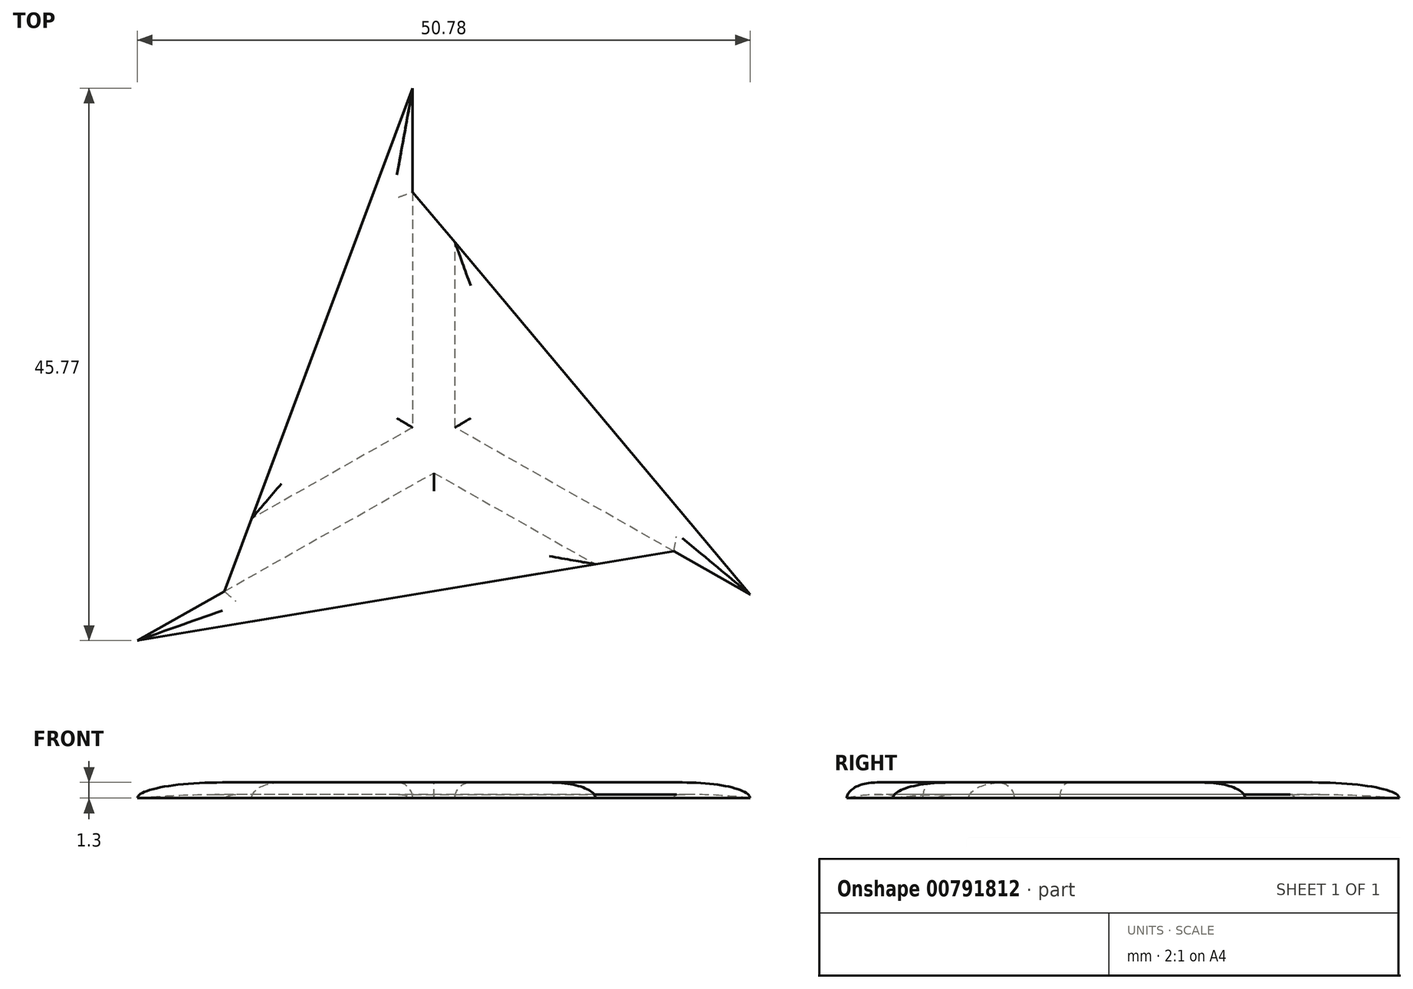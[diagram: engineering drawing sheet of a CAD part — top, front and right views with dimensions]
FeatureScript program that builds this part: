
annotation { "Feature Type Name" : "Feature", "Feature Type Description" : "" }
export const myFeature = defineFeature(function(context is Context, id is Id, definition is map)
    precondition{}
    {
        {
            var Q0;
            Q0=qCreatedBy(makeId("Top.planeOp"),FACE);
            var sketch = newSketch(context, id + "F0", { "sketchPlane" : qUnion([Q0])});
            skLineSegment(sketch, "E0.0", {"start": v(-37.37, 14.16) * mm, "end": v(-24.02, 49.82) * mm});
            skLineSegment(sketch, "E0.1", {"start": v(-24.02, 21.71) * mm, "end": v(-37.37, 14.16) * mm});
            skLineSegment(sketch, "E0.2", {"start": v(-24.02, 49.82) * mm, "end": v(-24.02, 21.71) * mm});
            skLineSegment(sketch, "E1.0", {"start": v(-20.52, 21.71) * mm, "end": v(-20.52, 37.04) * mm});
            skLineSegment(sketch, "E1.1", {"start": v(3.94, 7.87) * mm, "end": v(-20.52, 21.71) * mm});
            skLineSegment(sketch, "E1.2", {"start": v(-20.52, 37.04) * mm, "end": v(3.94, 7.87) * mm});
            skLineSegment(sketch, "E2.0", {"start": v(-46.84, 4.05) * mm, "end": v(-22.27, 17.95) * mm});
            skLineSegment(sketch, "E2.1", {"start": v(-8.87, 10.37) * mm, "end": v(-46.84, 4.05) * mm});
            skLineSegment(sketch, "E2.2", {"start": v(-22.27, 17.95) * mm, "end": v(-8.87, 10.37) * mm});
            skSolve(sketch);
        }
        {
            var Q0;
            Q0=qSketchRegion(id+"F0",true);
            extrude(context, id + "F1", {"entities" : qUnion([Q0]), "depth" : 1.3 * mm, "offsetDistance" : 25 * mm});
        }
        {
            var Q0;
            Q0=makeQuery(id+"F1.opExtrude","CAP_FACE",FACE,{"disambiguationData":[OSD([sQuery(id+"F0.wireOp",EDGE,"E0.0"),sQuery(id+"F0.wireOp",EDGE,"E0.1"),sQuery(id+"F0.wireOp",EDGE,"E0.2")])],"isStart":false});
            var Q1;
            Q1=makeQuery(id+"F1.opExtrude","CAP_FACE",FACE,{"disambiguationData":[OSD([sQuery(id+"F0.wireOp",EDGE,"E1.0"),sQuery(id+"F0.wireOp",EDGE,"E1.1"),sQuery(id+"F0.wireOp",EDGE,"E1.2")])],"isStart":false});
            var Q2;
            Q2=makeQuery(id+"F1.opExtrude","CAP_FACE",FACE,{"disambiguationData":[OSD([sQuery(id+"F0.wireOp",EDGE,"E2.0"),sQuery(id+"F0.wireOp",EDGE,"E2.1"),sQuery(id+"F0.wireOp",EDGE,"E2.2")])],"isStart":false});
            fillet(context, id + "F2", {"entities" : qUnion([Q0, Q1, Q2]), "radius" : 1.3 * mm, "tangentPropagation" : true, "allowEdgeOverflow" : false});
        }
        {
            var Q0;
            Q0=makeQuery(id+"F1.opExtrude","CAP_FACE",FACE,{"disambiguationData":[OSD([sQuery(id+"F0.wireOp",EDGE,"E0.0"),sQuery(id+"F0.wireOp",EDGE,"E0.1"),sQuery(id+"F0.wireOp",EDGE,"E0.2")])],"isStart":true});
            var sketch = newSketch(context, id + "F3", { "sketchPlane" : qUnion([Q0])});
            skLineSegment(sketch, "E3", {"start": v(-24.02, -49.82) * mm, "end": v(-39.63, -8.13) * mm});
            skLineSegment(sketch, "E4", {"start": v(-39.63, -8.13) * mm, "end": v(-46.84, -4.05) * mm});
            skLineSegment(sketch, "E5", {"start": v(-46.84, -4.05) * mm, "end": v(-8.87, -10.37) * mm});
            skLineSegment(sketch, "E6", {"start": v(-8.87, -10.37) * mm, "end": v(-2.4, -11.45) * mm});
            skLineSegment(sketch, "E7", {"start": v(-2.4, -11.45) * mm, "end": v(3.94, -7.87) * mm});
            skLineSegment(sketch, "E8", {"start": v(3.94, -7.87) * mm, "end": v(-20.52, -37.04) * mm});
            skLineSegment(sketch, "E9", {"start": v(-20.52, -37.04) * mm, "end": v(-24.02, -41.22) * mm});
            skLineSegment(sketch, "E10", {"start": v(-24.02, -41.22) * mm, "end": v(-24.02, -49.82) * mm});
            skSolve(sketch);
        }
        {
            var Q0;
            Q0=qSketchRegion(id+"F3",true);
            extrude(context, id + "F4", {"entities" : qUnion([Q0]), "oppositeDirection" : true, "depth" : 0.3 * mm, "offsetDistance" : 25 * mm});
        }
        {
            var Q0;
            Q0=makeQuery(id+"F4.opExtrude","CAP_FACE",FACE,{"disambiguationData":[OSD([sQuery(id+"F3.wireOp",EDGE,"E3"),sQuery(id+"F3.wireOp",EDGE,"E4"),sQuery(id+"F3.wireOp",EDGE,"E5"),sQuery(id+"F3.wireOp",EDGE,"E6"),sQuery(id+"F3.wireOp",EDGE,"E7"),sQuery(id+"F3.wireOp",EDGE,"E8"),sQuery(id+"F3.wireOp",EDGE,"E9"),sQuery(id+"F3.wireOp",EDGE,"E10")])],"isStart":false});
            fillet(context, id + "F5", {"entities" : qUnion([Q0]), "radius" : 2.5 * mm, "tangentPropagation" : true, "allowEdgeOverflow" : false});
        }
    });
